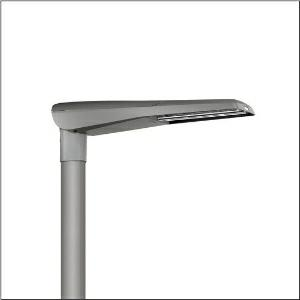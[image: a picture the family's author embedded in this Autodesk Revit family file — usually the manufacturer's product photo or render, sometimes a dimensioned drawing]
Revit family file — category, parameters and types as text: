
# Revit family: streetlight_sl_11_iq_mini___st1_0ab_5xc2nc1f08ge_aec6
name_source: partatom
category: Lighting Fixtures
units: mm (PartAtom-declared; Revit-internal decimal feet)

## family parameters
Cut with Voids When Loaded = No
Host = Face
Light Source = No
Part Type = Normal
Room Calculation Point = No
Round Connector Dimension = Use Diameter
Shared = No

## types (1)
- --- (1 x LED, 2430 lm, 25.3 W, 2200K)
    Apparent Load = 25 VA
    CIE Flux Codes = 29 63 95 100 100
    Color Rendering = 70
    Color Temperature = 2200K
    Default Elevation = 1800 mm
    Description = Streetlight SL 11 iQ mini, mast luminaire, primary light control with 3 zone facetted reflector, of plastic, silver coated, highly specular, primary optical cover: cover, of PMMA, transparent, light distribution: ST1.0aB, light emission: direct distribution, primary light characteristic: asymmetric, installation type: post-top, side-entry, lamps: LED, High Power LED, rated values: 2.860lm | 24,9W | 114,9lm/W (begin service life); end service life: 2.860lm | 25,7W; at 50% lumin. flux: 1.430lm | 12,8W | 111,7lm/W, colour temperature: 2200/2700/3000/4000K, colour rendering: CRI > 70, light colour: 722/727/730/740, light setting 1 begin service life: 100% | 2.860lm | 24,9W | 114,9lm/W | 3.000K, light setting 1 end service life: 25,7W, further light settings possible, control: Street-Remote, Auto-Match, Temp-Guard, Lumen-Switch, Night-Set, Smart-Wire, Light-Fading, Desk-Remote (wireless, voltage-free reading and setting of iQ features in the workshop via application-optimized NFC function/RFID function), optimised constant luminous flux control (CLO 2.0), with cable H07RN-F 5x 1.5mm², mains connection: 230..240V, AC, 50/60Hz, connection cable pre-assembled, cable length: 6,5m, luminaire housing, of diecast aluminium, powder-coated, Siteco® metallic grey (DB 702S), please order mast flange separately, inclination adjustable without tools: 0°, 5°, 10°, 15° (post-top) | 0°, -5°, -10°, -15° (side-entry), sealing non-destructively replaceable, multi-level sealing system, length: 736mm, width: 174mm, height: 116mm, mast flange for spigot size: 42mm (side-entry): 5XC10008XM4, 60/48mm (side-entry/post-top): 5XC10108XM2, 76/60mm (side-entry/post-top): 5XC10108XM1, equipment: standard, protection rating (complete): IP66, insulation class (complete): insulation class II (safety insulation), certification: CE, ENEC, ENEC+, VDE, impact resistance: IK10, permissible operating ambient temperature for outdoor applications: -25..+50°C, standard-compliant lighting for roads and squares, Environmental Product Declaration (EPD) tested and certified by an independent institute, packaging unit: 1 piece

Light Distribution: ST1.0aB
    Height = 116 mm
    Lamp = 1 x LED
    Lamp Light Flux = 2430 lm
    Lamp Power = 25.3 W
    Lamp count = 1
    Length = 736 mm
    Luminous efficacy = 96 lm/W
    Manufacturer = Siteco
    ModVariant = No
    Model = 5XC2NC1F08GE
    Number of Poles = 1
    OnlyDefault = Yes
    Power Factor = 1
    Product Name = Streetlight SL 11 iQ mini | ST1.0aB
    Product group = mast luminaire | pylon top
    ProductGroupID = 6100
    Protection Class = Protection class II
    Protection Degree = IP 66
    RLX_Detail_Level = 1
    RLX_Emergency_Light_Flux = 0 lm
    RLX_Emergency_Type = 0
    RLX_Emergency_Type_DB = No
    RlxData = <blob elided: 34785 chars, md5=a5122458>
    Socket = socket
    Standby Power = 0 W
    System Light Flux = 2430 lm
    System Power = 25 W
    Type Comments = individual setting: luminous flux: 100 % | dim-lin: 254 | 351 mA
    Type Image = l_1003508.jpg
    URL = http://relux.com
    VarID = @adj_002933
    Voltage = 0 V
    Weight = 0.00 kg
    Width = 174 mm

## geometry (parser evidence)
native form markers: Blend x4, Sweep x10
no freeform markers — native parametric forms only
